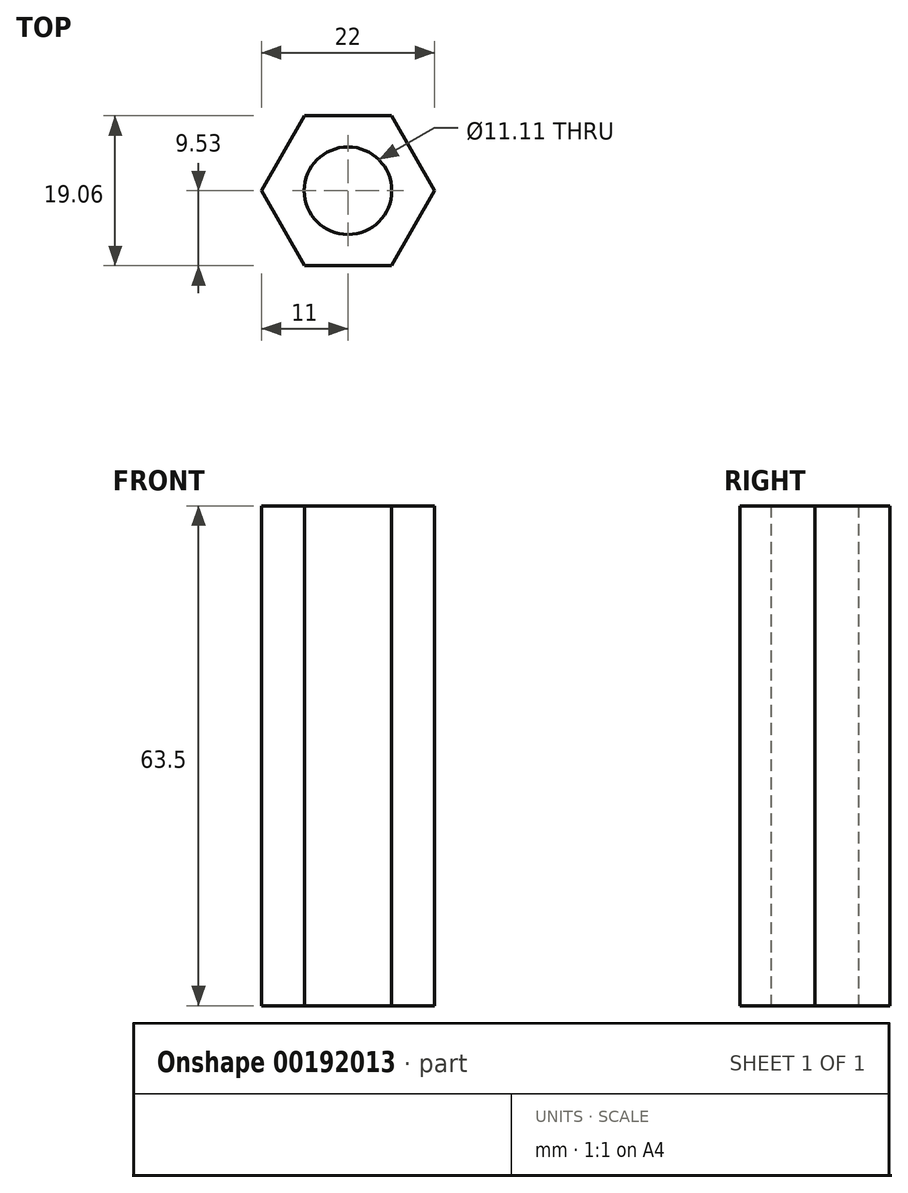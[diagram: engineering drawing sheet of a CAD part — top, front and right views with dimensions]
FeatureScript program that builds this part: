
annotation { "Feature Type Name" : "Feature", "Feature Type Description" : "" }
export const myFeature = defineFeature(function(context is Context, id is Id, definition is map)
    precondition{}
    {
        {
            var Q0;
            Q0=qCreatedBy(makeId("Top.planeOp"),FACE);
            var sketch = newSketch(context, id + "F0", { "sketchPlane" : qUnion([Q0])});
            skCircle(sketch, "E0.cCircle", {"center": v(0, 0) * mm, "radius": 9.53 * mm, "construction": true});
            skLineSegment(sketch, "E0.0", {"start": v(5.5, 9.53) * mm, "end": v(11, 0) * mm});
            skLineSegment(sketch, "E0.1", {"start": v(11, 0) * mm, "end": v(5.5, -9.52) * mm});
            skLineSegment(sketch, "E0.2", {"start": v(5.5, -9.53) * mm, "end": v(-5.5, -9.53) * mm});
            skLineSegment(sketch, "E0.3", {"start": v(-5.5, -9.53) * mm, "end": v(-11, 0) * mm});
            skLineSegment(sketch, "E0.4", {"start": v(-11, 0) * mm, "end": v(-5.5, 9.53) * mm});
            skLineSegment(sketch, "E0.5", {"start": v(-5.5, 9.52) * mm, "end": v(5.5, 9.53) * mm});
            skPoint(sketch, "E0.0.midPoint", {"position": v(8.25, 4.76) * mm});
            skCircle(sketch, "E1", {"center": v(0, 0) * mm, "radius": 5.56 * mm});
            skSolve(sketch);
        }
        {
            var Q0;
            Q0=makeQuery(id+"F0.imprint","IMPRINT",FACE,{"disambiguationData":[TD([[makeQuery(id+"F0.imprint","IMPRINT",EDGE,{"derivedFrom":sQuery(id+"F0.wireOp",EDGE,"E0.0")}),-1.0]])]});
            extrude(context, id + "F1", {"entities" : qUnion([Q0]), "depth" : 63.5 * mm});
        }
    });
